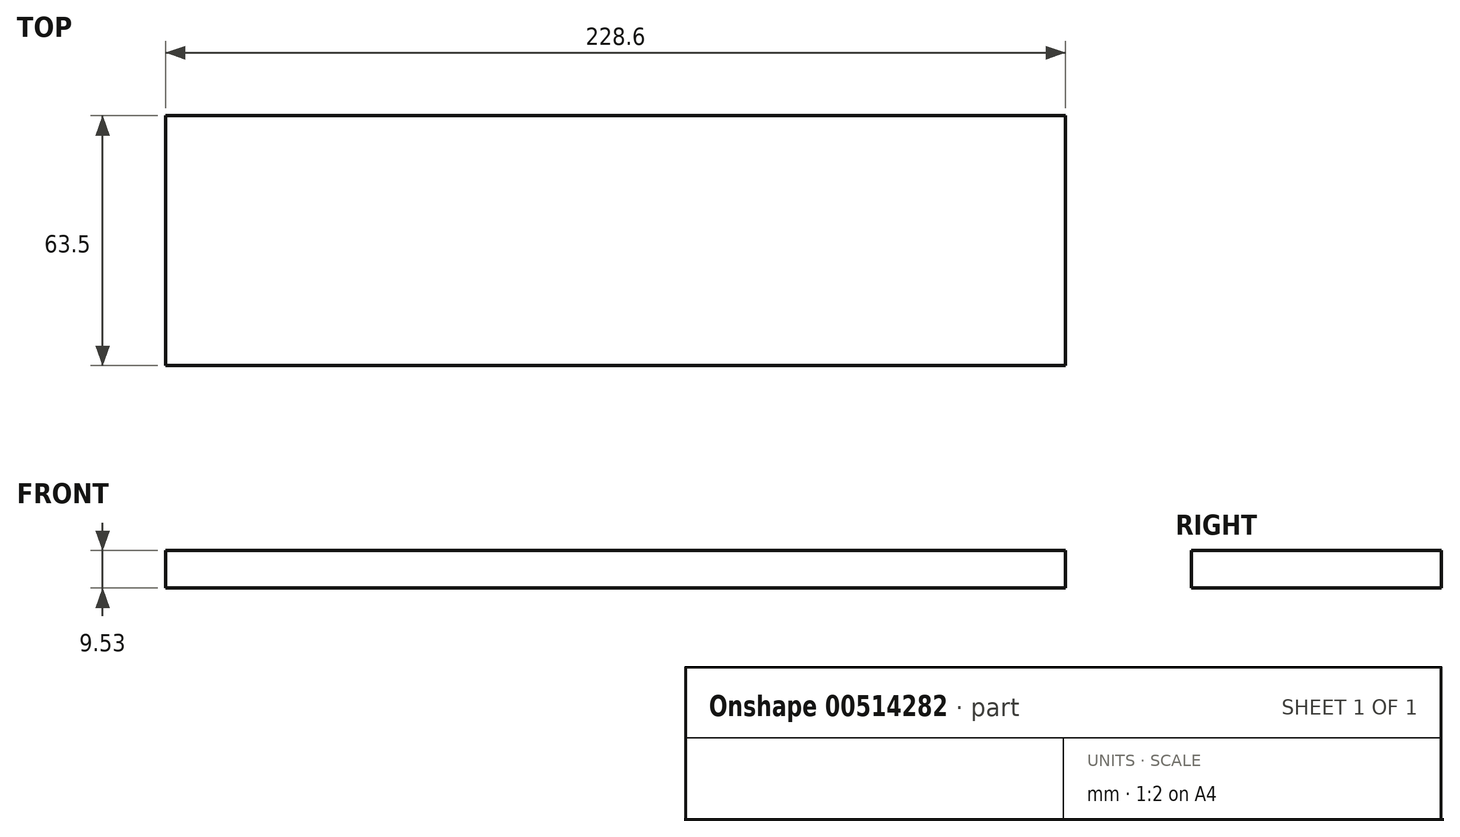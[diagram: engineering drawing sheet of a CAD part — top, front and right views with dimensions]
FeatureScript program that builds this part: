
annotation { "Feature Type Name" : "Feature", "Feature Type Description" : "" }
export const myFeature = defineFeature(function(context is Context, id is Id, definition is map)
    precondition{}
    {
        {
            var Q0;
            Q0=qCreatedBy(makeId("Top.planeOp"),FACE);
            var sketch = newSketch(context, id + "F0", { "sketchPlane" : qUnion([Q0])});
            skLineSegment(sketch, "E0.bottom", {"start": v(114.3, -31.75) * mm, "end": v(-114.3, -31.75) * mm});
            skLineSegment(sketch, "E0.top", {"start": v(114.3, 31.75) * mm, "end": v(-114.3, 31.75) * mm});
            skLineSegment(sketch, "E0.left", {"start": v(114.3, -31.75) * mm, "end": v(114.3, 31.75) * mm});
            skLineSegment(sketch, "E0.right", {"start": v(-114.3, -31.75) * mm, "end": v(-114.3, 31.75) * mm});
            skPoint(sketch, "E0.middle", {"position": v(0, 0) * mm});
            skSolve(sketch);
        }
        {
            var Q0;
            Q0 = qSketchRegion(id + "F0", true);
            extrude(context, id + "F1", {"entities" : qUnion([Q0]), "depth" : 9.52 * mm});
        }
    });
